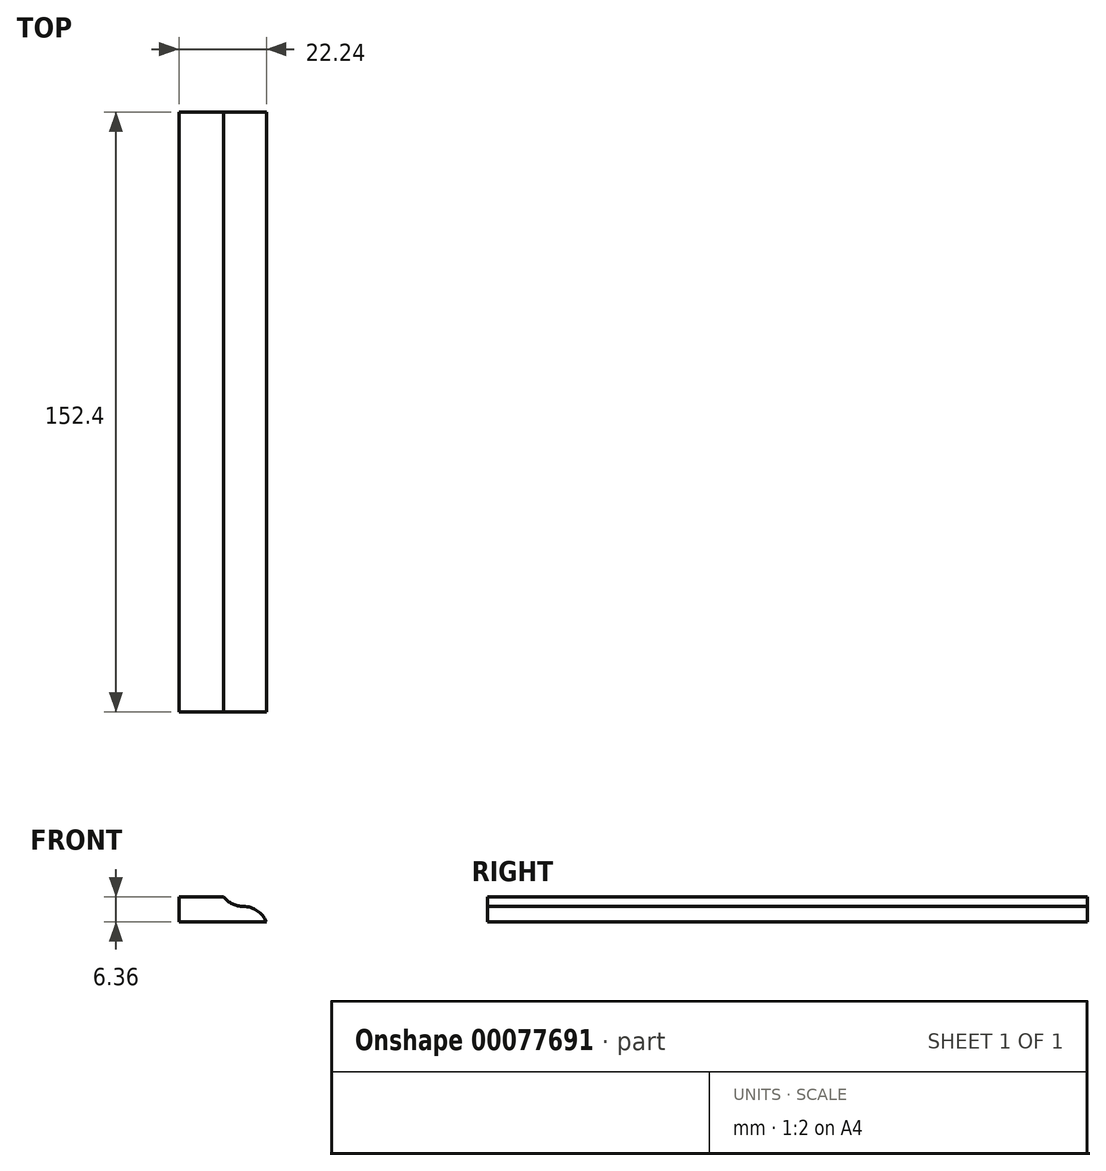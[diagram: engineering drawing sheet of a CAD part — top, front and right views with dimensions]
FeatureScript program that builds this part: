
annotation { "Feature Type Name" : "Feature", "Feature Type Description" : "" }
export const myFeature = defineFeature(function(context is Context, id is Id, definition is map)
    precondition{}
    {
        {
            var Q0;
            Q0=qCreatedBy(makeId("Front.planeOp"),FACE);
            var sketch = newSketch(context, id + "F0", { "sketchPlane" : qUnion([Q0])});
            skLineSegment(sketch, "E0", {"start": v(-11.12, 3.18) * mm, "end": v(-11.12, -3.18) * mm});
            skLineSegment(sketch, "E1", {"start": v(-11.12, -3.18) * mm, "end": v(11.12, -3.18) * mm});
            skLineSegment(sketch, "E2", {"start": v(-11.12, 3.18) * mm, "end": v(0.25, 3.18) * mm});
            skArc(sketch, "E3", {"start": v(11.12, -3.18) * mm, "mid": v(8.78, -0.33) * mm, "end": v(5.25, 0.74) * mm});
            skArc(sketch, "E4", {"start": v(0.25, 3.18) * mm, "mid": v(2.47, 1.38) * mm, "end": v(5.25, 0.74) * mm});
            skSolve(sketch);
        }
        {
            var Q0;
            Q0=makeQuery(id+"F0.imprint","IMPRINT",FACE,{"disambiguationData":[TD([[makeQuery(id+"F0.imprint","IMPRINT",EDGE,{"derivedFrom":sQuery(id+"F0.wireOp",EDGE,"E0")}),1.0]])]});
            extrude(context, id + "F1", {"entities" : qUnion([Q0]), "depth" : 152.4 * mm});
        }
    });
